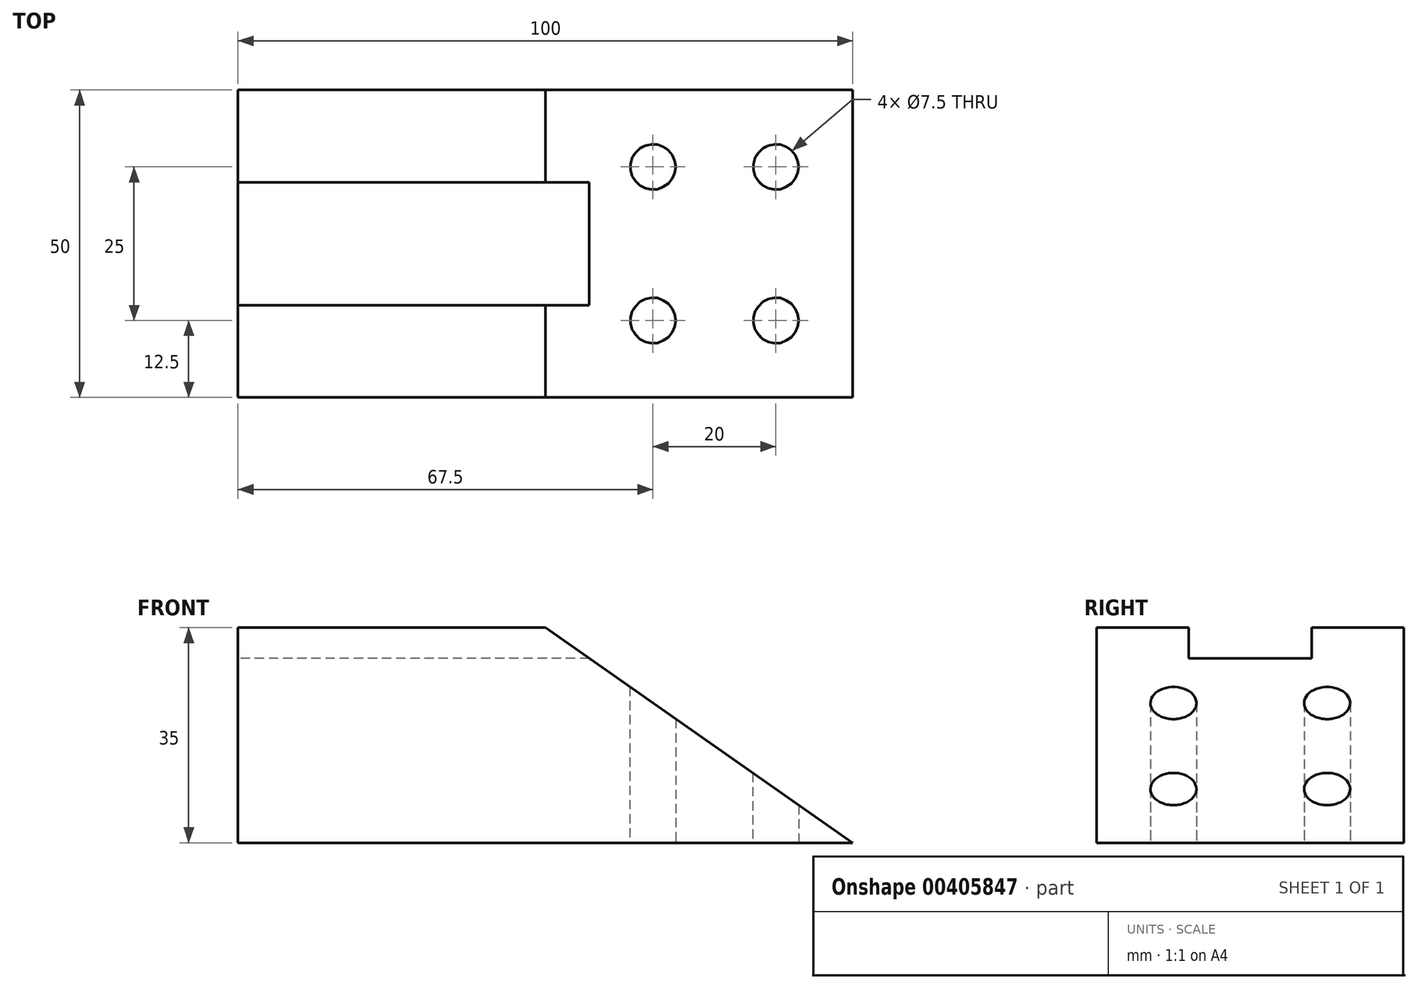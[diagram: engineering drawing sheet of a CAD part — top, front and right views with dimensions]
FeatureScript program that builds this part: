
annotation { "Feature Type Name" : "Feature", "Feature Type Description" : "" }
export const myFeature = defineFeature(function(context is Context, id is Id, definition is map)
    precondition{}
    {
        {
            var Q0;
            Q0=qCreatedBy(makeId("Top.planeOp"),FACE);
            var sketch = newSketch(context, id + "F0", { "sketchPlane" : qUnion([Q0])});
            skLineSegment(sketch, "E0.bottom", {"start": v(-50, 25) * mm, "end": v(50, 25) * mm});
            skLineSegment(sketch, "E0.top", {"start": v(-50, -25) * mm, "end": v(50, -25) * mm});
            skLineSegment(sketch, "E0.left", {"start": v(-50, 25) * mm, "end": v(-50, -25) * mm});
            skLineSegment(sketch, "E0.right", {"start": v(50, 25) * mm, "end": v(50, -25) * mm});
            skPoint(sketch, "E0.middle", {"position": v(0, 0) * mm});
            skCircle(sketch, "E1", {"center": v(17.5, -12.5) * mm, "radius": 3.75 * mm});
            skCircle(sketch, "E2", {"center": v(17.5, 12.5) * mm, "radius": 3.75 * mm});
            skCircle(sketch, "E3", {"center": v(37.5, 12.5) * mm, "radius": 3.75 * mm});
            skCircle(sketch, "E4", {"center": v(37.5, -12.5) * mm, "radius": 3.75 * mm});
            skLineSegment(sketch, "E5.bottom", {"start": v(0, -25) * mm, "end": v(15, -25) * mm});
            skLineSegment(sketch, "E5.top", {"start": v(0, -35) * mm, "end": v(15, -35) * mm});
            skLineSegment(sketch, "E5.left", {"start": v(0, -25) * mm, "end": v(0, -35) * mm});
            skLineSegment(sketch, "E5.right", {"start": v(15, -25) * mm, "end": v(15, -35) * mm});
            skSolve(sketch);
        }
        {
            var Q0;
            Q0=makeQuery(id+"F0.imprint","IMPRINT",FACE,{"disambiguationData":[TD([[makeQuery(id+"F0.imprint","IMPRINT",EDGE,{"derivedFrom":sQuery(id+"F0.wireOp",EDGE,"E0.bottom")}),-1.0]])]});
            var Q1;
            Q1=makeQuery(id+"F0.imprint","IMPRINT",FACE,{"disambiguationData":[TD([[makeQuery(id+"F0.imprint","IMPRINT",EDGE,{"derivedFrom":sQuery(id+"F0.wireOp",EDGE,"E5.bottom")}),-1.0]])]});
            extrude(context, id + "F1", {"entities" : qUnion([Q0, Q1]), "depth" : 35 * mm});
        }
        {
            var Q0;
            Q0=makeQuery(id+"F1.opExtrude","SWEPT_FACE",FACE,{"disambiguationData":[OSD([sQuery(id+"F0.wireOp",EDGE,"E0.bottom")])]});
            var sketch = newSketch(context, id + "F2", { "sketchPlane" : qUnion([Q0])});
            skPoint(sketch, "E6.0", {"position": v(0, 35) * mm});
            skLineSegment(sketch, "E7", {"start": v(-50, 0) * mm, "end": v(0, 35) * mm});
            skSolve(sketch);
        }
        {
            var Q0;
            {var subQ0=sQuery(id+"F2.wireOp",EDGE,"E7");Q0=makeQuery(id+"F2.imprint","IMPRINT",FACE,{"disambiguationData":[TD([[makeQuery(id+"F2.imprint","IMPRINT",EDGE,{"derivedFrom":subQ0}),1.0]])]});}
            extrude(context, id + "F3", {"entities" : qUnion([Q0]), "operationType" : NewBodyOperationType.REMOVE, "endBound" : BoundingType.THROUGH_ALL, "oppositeDirection" : true, "depth" : 25 * mm});
        }
        {
            var Q0;
            Q0=makeQuery(id+"F1.opExtrude","SWEPT_FACE",FACE,{"disambiguationData":[OSD([sQuery(id+"F0.wireOp",EDGE,"E0.left")])]});
            var sketch = newSketch(context, id + "F4", { "sketchPlane" : qUnion([Q0])});
            skLineSegment(sketch, "E8.bottom", {"start": v(-10, 40) * mm, "end": v(10, 40) * mm});
            skLineSegment(sketch, "E8.top", {"start": v(-10, 30) * mm, "end": v(10, 30) * mm});
            skLineSegment(sketch, "E8.left", {"start": v(-10, 40) * mm, "end": v(-10, 30) * mm});
            skLineSegment(sketch, "E8.right", {"start": v(10, 40) * mm, "end": v(10, 30) * mm});
            skPoint(sketch, "E8.middle", {"position": v(0, 35) * mm});
            skSolve(sketch);
        }
        {
            var Q0;
            {var subQ0=sQuery(id+"F4.wireOp",EDGE,"E8.top");Q0=makeQuery(id+"F4.imprint","IMPRINT",FACE,{"disambiguationData":[TD([[makeQuery(id+"F4.imprint","IMPRINT",EDGE,{"derivedFrom":subQ0}),1.0]])]});}
            extrude(context, id + "F5", {"entities" : qUnion([Q0]), "operationType" : NewBodyOperationType.REMOVE, "endBound" : BoundingType.THROUGH_ALL, "oppositeDirection" : true, "depth" : 25 * mm});
        }
    });
